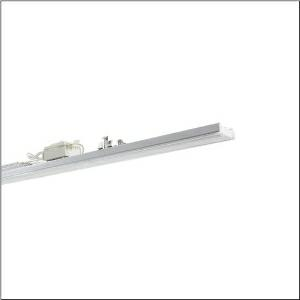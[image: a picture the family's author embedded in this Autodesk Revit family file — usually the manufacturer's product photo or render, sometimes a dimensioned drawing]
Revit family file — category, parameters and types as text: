
# Revit family: licross_r__21_recessed_mo_52tl10mn4a5g_0eff
name_source: partatom
category: Lighting Fixtures
units: mm (PartAtom-declared; Revit-internal decimal feet)

## family parameters
Cut with Voids When Loaded = No
Host = Face
Light Source = No
Part Type = Normal
Room Calculation Point = No
Round Connector Dimension = Use Diameter
Shared = No

## types (1)
- --- (1 x LED, 10690 lm, 60.5 W, 4000K)
    Apparent Load = 61 VA
    CIE Flux Codes = 50 81 96 100 100
    Color Rendering = 80
    Color Temperature = 4000K
    Default Elevation = 1800 mm
    Description = Licross® 21 Recessed MO, luminaire insert, of sheet steel, galvanised, coil coated, white, length: 1.500mm, width: 66mm, height: 67mm, LED rated luminous flux: 10.690lm, light colour: 840, control gear: ON/OFF Multilumen, with plug, 3-pole, with phase selection, mains connection: 220..240V, AC, 50/60Hz, rated input power: 61W, internal wiring halogen-free, primary optical cover: cover, of PMMA, light emission: direct distribution, primary light characteristic: symmetric, protection rating (complete): IP40, insulation class (complete): insulation class I (protective earthing), certification: CE, ENEC, VDE, UKCA, protection symbol: D if used in an environment without relevant dust loads with corresponding accessories, impact resistance: IK06, permissible ambient temperature for indoor applications: -35..+40°C, corresponds to IFS (International Featured Standards) requirements for safety and quality in the food industry, reducing of maximum allowable ambient temperature of 5°C with ceiling mounting, LABS conformity tested according to VDMA 24364:2018-05, packaging unit: 1 piece
    Height = 58 mm
    Lamp = 1 x LED
    Lamp Light Flux = 10690 lm
    Lamp Power = 60.5 W
    Lamp count = 1
    Length = 1500 mm
    Luminous efficacy = 177 lm/W
    Manufacturer = Siteco
    ModVariant = No
    Model = 52TL10MN4A5G
    Mounting Place = Ceiling
    Mounting Type = Pendant
    Number of Poles = 1
    OnlyDefault = Yes
    Power Factor = 1
    Product Name = Licross® 21 Recessed MO
    Product group = luminaire insert | ceiling pendant
    ProductGroupID = 902
    Protection Class = Protection class I
    Protection Degree = IP 40
    RLX_Detail_Level = 1
    RLX_Emergency_Light_Flux = 0 lm
    RLX_Emergency_Type = 0
    RLX_Emergency_Type_DB = No
    RlxData = <blob elided: 22153 chars, md5=7a1336cb>
    Socket = socket
    Standby Power = 0 W
    System Light Flux = 10690 lm
    System Power = 61 W
    Type Comments = factory setting: luminous flux: 100 % | (A | C | E) | 140 mA
    Type Image = l_1296930.jpg
    URL = http://relux.com
    VarID = @adj_129515
    Voltage = 0 V
    Weight = 0.00 kg
    Width = 66 mm

## geometry (parser evidence)
native form markers: Blend x4, Sweep x11
no freeform markers — native parametric forms only
